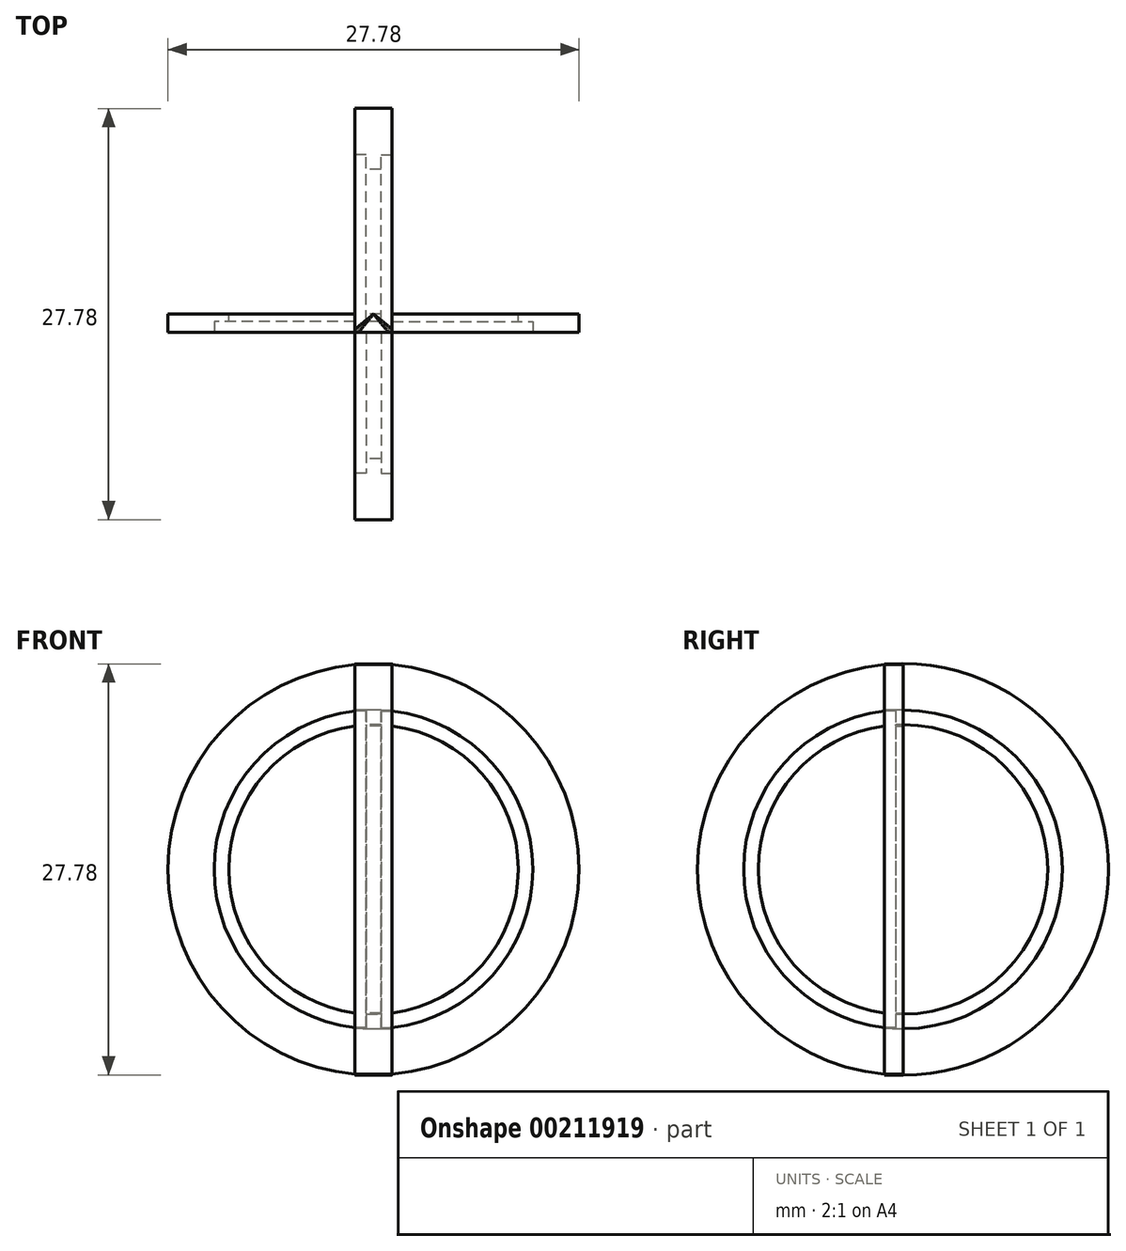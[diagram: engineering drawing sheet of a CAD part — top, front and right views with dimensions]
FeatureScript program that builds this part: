
annotation { "Feature Type Name" : "Feature", "Feature Type Description" : "" }
export const myFeature = defineFeature(function(context is Context, id is Id, definition is map)
    precondition{}
    {
        {
            assignVariable(context, id + "F0", {"name" : "LengthAxial", "anyValue" : 1.25});
        }
        {
            assignVariable(context, id + "F1", {"name" : "Relief", "anyValue" : .75});
        }
        {
            var Q0;
            Q0=qCreatedBy(makeId("Right.planeOp"),FACE);
            var sketch = newSketch(context, id + "F2", { "sketchPlane" : qUnion([Q0])});
            skCircle(sketch, "E0", {"center": v(0, 0) * mm, "radius": 13.9 * mm});
            skSolve(sketch);
        }
        {
            var Q0;
            Q0=qCreatedBy(makeId("Front.planeOp"),FACE);
            var sketch = newSketch(context, id + "F3", { "sketchPlane" : qUnion([Q0])});
            skCircle(sketch, "E1", {"center": v(0, 0) * mm, "radius": 13.9 * mm});
            skSolve(sketch);
        }
        {
            var Q0;
            Q0=qCreatedBy(makeId("Right.planeOp"),FACE);
            var sketch = newSketch(context, id + "F4", { "sketchPlane" : qUnion([Q0])});
            skCircle(sketch, "E2", {"center": v(0, 0) * mm, "radius": 9.78 * mm});
            skSolve(sketch);
        }
        {
            var Q0;
            Q0=qCreatedBy(makeId("Front.planeOp"),FACE);
            var sketch = newSketch(context, id + "F5", { "sketchPlane" : qUnion([Q0])});
            skCircle(sketch, "E3", {"center": v(0, 0) * mm, "radius": 9.78 * mm});
            skSolve(sketch);
        }
        {
            var Q0;
            Q0=makeQuery(id+"F2.imprint","IMPRINT",FACE,{"disambiguationData":[TD([[makeQuery(id+"F2.imprint","IMPRINT",EDGE,{"derivedFrom":sQuery(id+"F2.wireOp",EDGE,"E0")}),1.0]])]});
            var Q1;
            Q1=sQuery(id+"F2.wireOp",EDGE,"E0");
            extrude(context, id + "F6", {"entities" : qUnion([Q0]), "surfaceEntities" : qUnion([Q1]), "depth" : (getVariable(context, 'LengthAxial')) * mm, "hasSecondDirection" : true, "secondDirectionOppositeDirection" : true, "secondDirectionDepth" : (getVariable(context, 'LengthAxial')) * mm});
        }
        {
            var Q0;
            Q0=makeQuery(id+"F3.imprint","IMPRINT",FACE,{"disambiguationData":[TD([[makeQuery(id+"F3.imprint","IMPRINT",EDGE,{"derivedFrom":sQuery(id+"F3.wireOp",EDGE,"E1")}),1.0]])]});
            extrude(context, id + "F7", {"entities" : qUnion([Q0]), "depth" : (getVariable(context, 'LengthAxial')) * mm});
        }
        {
            var Q0;
            Q0=makeQuery(id+"F7.opExtrude","SWEPT_BODY",BODY,{"disambiguationData":[OSD([sQuery(id+"F3.wireOp",EDGE,"E1")])]});
            var Q1;
            Q1=makeQuery(id+"F6.opExtrude","SWEPT_BODY",BODY,{"disambiguationData":[OSD([sQuery(id+"F2.wireOp",EDGE,"E0")])]});
            booleanBodies(context, id + "F8", {"operationType" : BooleanOperationType.UNION, "tools" : qUnion([Q0, Q1])});
        }
        {
            var Q0;
            Q0=qSketchRegion(id+"F4",true);
            extrude(context, id + "F9", {"entities" : qUnion([Q0]), "depth" : (getVariable(context, 'LengthAxial')) * mm, "hasSecondDirection" : true, "secondDirectionOppositeDirection" : true, "secondDirectionDepth" : (getVariable(context, 'LengthAxial')) * mm});
        }
        {
            var Q0;
            Q0=makeQuery(id+"F5.imprint","IMPRINT",FACE,{"disambiguationData":[TD([[makeQuery(id+"F5.imprint","IMPRINT",EDGE,{"derivedFrom":sQuery(id+"F5.wireOp",EDGE,"E3")}),1.0]])]});
            extrude(context, id + "F10", {"entities" : qUnion([Q0]), "depth" : (getVariable(context, 'LengthAxial')) * mm});
        }
        {
            var Q0;
            Q0=makeQuery(id+"F9.opExtrude","SWEPT_BODY",BODY,{"disambiguationData":[OSD([sQuery(id+"F4.wireOp",EDGE,"E2")])]});
            var Q1;
            Q1=makeQuery(id+"F7.opExtrude","SWEPT_BODY",BODY,{"disambiguationData":[OSD([sQuery(id+"F3.wireOp",EDGE,"E1")])]});
            booleanBodies(context, id + "F11", {"operationType" : BooleanOperationType.SUBTRACTION, "tools" : qUnion([Q0]), "targets" : qUnion([Q1])});
        }
        {
            var Q0;
            Q0=makeQuery(id+"F6.opExtrude","CAP_FACE",FACE,{"disambiguationData":[OSD([sQuery(id+"F2.wireOp",EDGE,"E0")])],"isStart":false});
            var sketch = newSketch(context, id + "F12", { "sketchPlane" : qUnion([Q0])});
            skCircle(sketch, "E4", {"center": v(0, 0) * mm, "radius": 10.77 * mm});
            skSolve(sketch);
        }
        {
            var Q0;
            Q0=makeQuery(id+"F7.opExtrude","CAP_FACE",FACE,{"disambiguationData":[OSD([sQuery(id+"F3.wireOp",EDGE,"E1")])],"isStart":false});
            var sketch = newSketch(context, id + "F13", { "sketchPlane" : qUnion([Q0])});
            skCircle(sketch, "E5", {"center": v(0, 0) * mm, "radius": 10.77 * mm});
            skSolve(sketch);
        }
        {
            var Q0;
            Q0=makeQuery(id+"F6.opExtrude","CAP_FACE",FACE,{"disambiguationData":[OSD([sQuery(id+"F2.wireOp",EDGE,"E0")])],"isStart":true});
            var sketch = newSketch(context, id + "F14", { "sketchPlane" : qUnion([Q0])});
            skCircle(sketch, "E6", {"center": v(0, 0) * mm, "radius": 10.77 * mm});
            skSolve(sketch);
        }
        {
            var Q0;
            Q0=makeQuery(id+"F12.imprint","IMPRINT",FACE,{"disambiguationData":[TD([[makeQuery(id+"F12.imprint","IMPRINT",EDGE,{"derivedFrom":sQuery(id+"F12.wireOp",EDGE,"E4")}),1.0]])]});
            extrude(context, id + "F15", {"entities" : qUnion([Q0]), "operationType" : NewBodyOperationType.REMOVE, "oppositeDirection" : true, "depth" : (getVariable(context, 'Relief')) * mm});
        }
        {
            var Q0;
            Q0=makeQuery(id+"F13.imprint","IMPRINT",FACE,{"disambiguationData":[TD([[makeQuery(id+"F13.imprint","IMPRINT",EDGE,{"derivedFrom":sQuery(id+"F13.wireOp",EDGE,"E5")}),1.0]])]});
            extrude(context, id + "F16", {"entities" : qUnion([Q0]), "operationType" : NewBodyOperationType.REMOVE, "oppositeDirection" : true, "depth" : (getVariable(context, 'Relief')) * mm});
        }
        {
            var Q0;
            Q0=makeQuery(id+"F14.imprint","IMPRINT",FACE,{"disambiguationData":[TD([[makeQuery(id+"F14.imprint","IMPRINT",EDGE,{"derivedFrom":sQuery(id+"F14.wireOp",EDGE,"E6")}),1.0]])]});
            extrude(context, id + "F17", {"entities" : qUnion([Q0]), "operationType" : NewBodyOperationType.REMOVE, "oppositeDirection" : true, "depth" : (getVariable(context, 'Relief')) * mm});
        }
        {
            var Q0;
            Q0=makeQuery(id+"FOWGCQSV9ENfEy0_3.opBoolean","INTERSECT",EDGE,{"derivedFrom":[makeQuery(id+"Fn0R11ubkhZaJAg_1.opExtrude","SWEPT_FACE",FACE,{"disambiguationData":[OSD([sQuery(id+"FdTQ3dJKm3ek1Nl_0.wireOp",EDGE,"PZkoudbQ-ZCWl-3RD1-L5qw-VDIZXBaiUssr")])]}),makeQuery(id+"F7.opExtrude","SWEPT_FACE",FACE,{"disambiguationData":[OSD([sQuery(id+"F3.wireOp",EDGE,"E1")])]})]});
            var Q1;
            Q1=makeQuery(id+"FOWGCQSV9ENfEy0_3.opBoolean","INTERSECT",EDGE,{"derivedFrom":[makeQuery(id+"Fn0R11ubkhZaJAg_1.opExtrude","SWEPT_FACE",FACE,{"disambiguationData":[OSD([sQuery(id+"FdTQ3dJKm3ek1Nl_0.wireOp",EDGE,"PZkoudbQ-ZCWl-3RD1-L5qw-VDIZXBaiUssr")])]}),makeQuery(id+"F6.opExtrude","SWEPT_FACE",FACE,{"disambiguationData":[OSD([sQuery(id+"F2.wireOp",EDGE,"E0")])]})]});
            var Q2;
            Q2=makeQuery(id+"F8.opBoolean","INTERSECT",EDGE,{"derivedFrom":[makeQuery(id+"F6.opExtrude","SWEPT_FACE",FACE,{"disambiguationData":[OSD([sQuery(id+"F2.wireOp",EDGE,"E0")])]}),makeQuery(id+"F7.opExtrude","SWEPT_FACE",FACE,{"disambiguationData":[OSD([sQuery(id+"F3.wireOp",EDGE,"E1")])]})]});
            fillet(context, id + "F18", {"entities" : qUnion([Q0, Q1, Q2]), "radius" : 3.17 * mm, "tangentPropagation" : true, "allowEdgeOverflow" : false});
        }
    });
